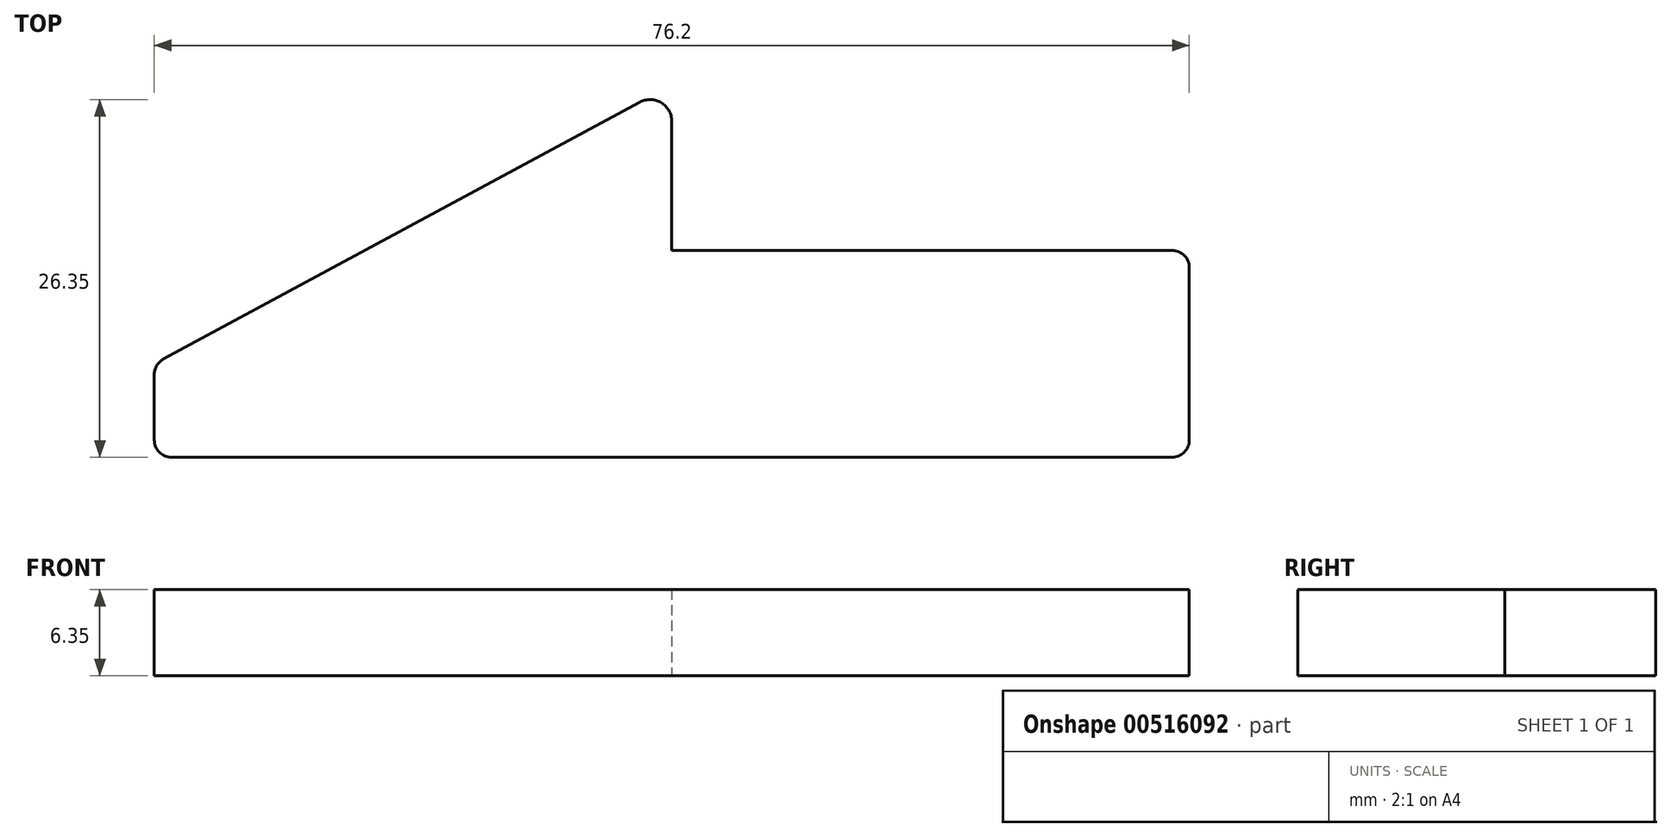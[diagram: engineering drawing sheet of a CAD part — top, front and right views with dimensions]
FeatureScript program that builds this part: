
annotation { "Feature Type Name" : "Feature", "Feature Type Description" : "" }
export const myFeature = defineFeature(function(context is Context, id is Id, definition is map)
    precondition{}
    {
        {
            var Q0;
            Q0=qCreatedBy(makeId("Top.planeOp"),FACE);
            var sketch = newSketch(context, id + "F0", { "sketchPlane" : qUnion([Q0])});
            skLineSegment(sketch, "E0", {"start": v(51.68, 18.9) * mm, "end": v(14.85, 18.9) * mm});
            skLineSegment(sketch, "E1", {"start": v(14.85, 18.9) * mm, "end": v(14.85, 28.41) * mm});
            skLineSegment(sketch, "E2", {"start": v(52.95, 17.63) * mm, "end": v(52.95, 4.93) * mm});
            skLineSegment(sketch, "E3", {"start": v(51.68, 3.66) * mm, "end": v(-21.98, 3.66) * mm});
            skLineSegment(sketch, "E4", {"start": v(-23.25, 4.93) * mm, "end": v(-23.25, 9.76) * mm});
            skLineSegment(sketch, "E5", {"start": v(-22.58, 10.88) * mm, "end": v(12.5, 29.82) * mm});
            skPoint(sketch, "E6.visualSharp", {"position": v(14.85, 31.1) * mm});
            skArc(sketch, "E6.filletArc", {"start": v(14.85, 28.41) * mm, "mid": v(14.07, 29.79) * mm, "end": v(12.5, 29.82) * mm});
            skPoint(sketch, "E7.visualSharp", {"position": v(-23.25, 10.52) * mm});
            skArc(sketch, "E7.filletArc", {"start": v(-22.58, 10.88) * mm, "mid": v(-23.07, 10.42) * mm, "end": v(-23.25, 9.76) * mm});
            skPoint(sketch, "E8.visualSharp", {"position": v(52.95, 3.66) * mm});
            skArc(sketch, "E8.filletArc", {"start": v(51.68, 3.66) * mm, "mid": v(52.58, 4.04) * mm, "end": v(52.95, 4.93) * mm});
            skPoint(sketch, "E9.visualSharp", {"position": v(52.95, 18.9) * mm});
            skArc(sketch, "E9.filletArc", {"start": v(52.95, 17.63) * mm, "mid": v(52.58, 18.53) * mm, "end": v(51.68, 18.9) * mm});
            skPoint(sketch, "E10.visualSharp", {"position": v(-23.25, 3.66) * mm});
            skArc(sketch, "E10.filletArc", {"start": v(-23.25, 4.93) * mm, "mid": v(-22.88, 4.04) * mm, "end": v(-21.98, 3.66) * mm});
            skSolve(sketch);
        }
        {
            var Q0;
            Q0=makeQuery(id+"F0.imprint","IMPRINT",FACE,{"disambiguationData":[TD([[makeQuery(id+"F0.imprint","IMPRINT",EDGE,{"derivedFrom":sQuery(id+"F0.wireOp",EDGE,"E0")}),1.0]])]});
            extrude(context, id + "F1", {"entities" : qUnion([Q0]), "depth" : 6.35 * mm, "offsetDistance" : 25.4 * mm});
        }
    });
